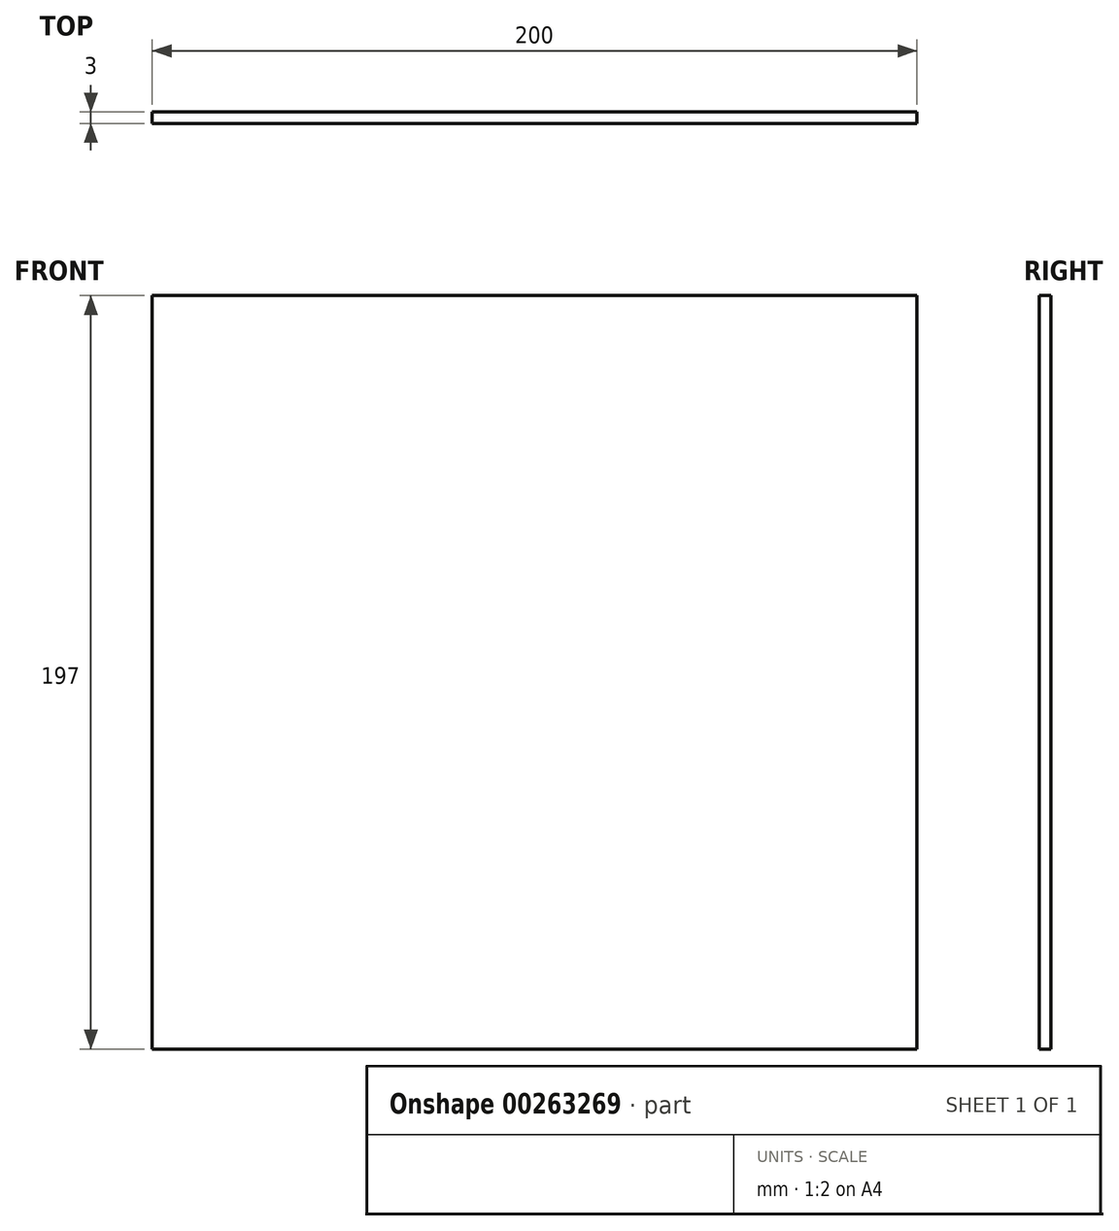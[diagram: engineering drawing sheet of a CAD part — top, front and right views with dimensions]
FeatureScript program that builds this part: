
annotation { "Feature Type Name" : "Feature", "Feature Type Description" : "" }
export const myFeature = defineFeature(function(context is Context, id is Id, definition is map)
    precondition{}
    {
        {
            var Q0;
            Q0=qCreatedBy(makeId("Front.planeOp"),FACE);
            var sketch = newSketch(context, id + "F0", { "sketchPlane" : qUnion([Q0])});
            skLineSegment(sketch, "E0.bottom", {"start": v(100, -98.5) * mm, "end": v(-100, -98.5) * mm});
            skLineSegment(sketch, "E0.top", {"start": v(100, 98.5) * mm, "end": v(-100, 98.5) * mm});
            skLineSegment(sketch, "E0.left", {"start": v(100, -98.5) * mm, "end": v(100, 98.5) * mm});
            skLineSegment(sketch, "E0.right", {"start": v(-100, -98.5) * mm, "end": v(-100, 98.5) * mm});
            skPoint(sketch, "E0.middle", {"position": v(0, 0) * mm});
            skSolve(sketch);
        }
        {
            var Q0;
            Q0 = qSketchRegion(id + "F0", true);
            extrude(context, id + "F1", {"entities" : qUnion([Q0]), "depth" : 3 * mm});
        }
    });
